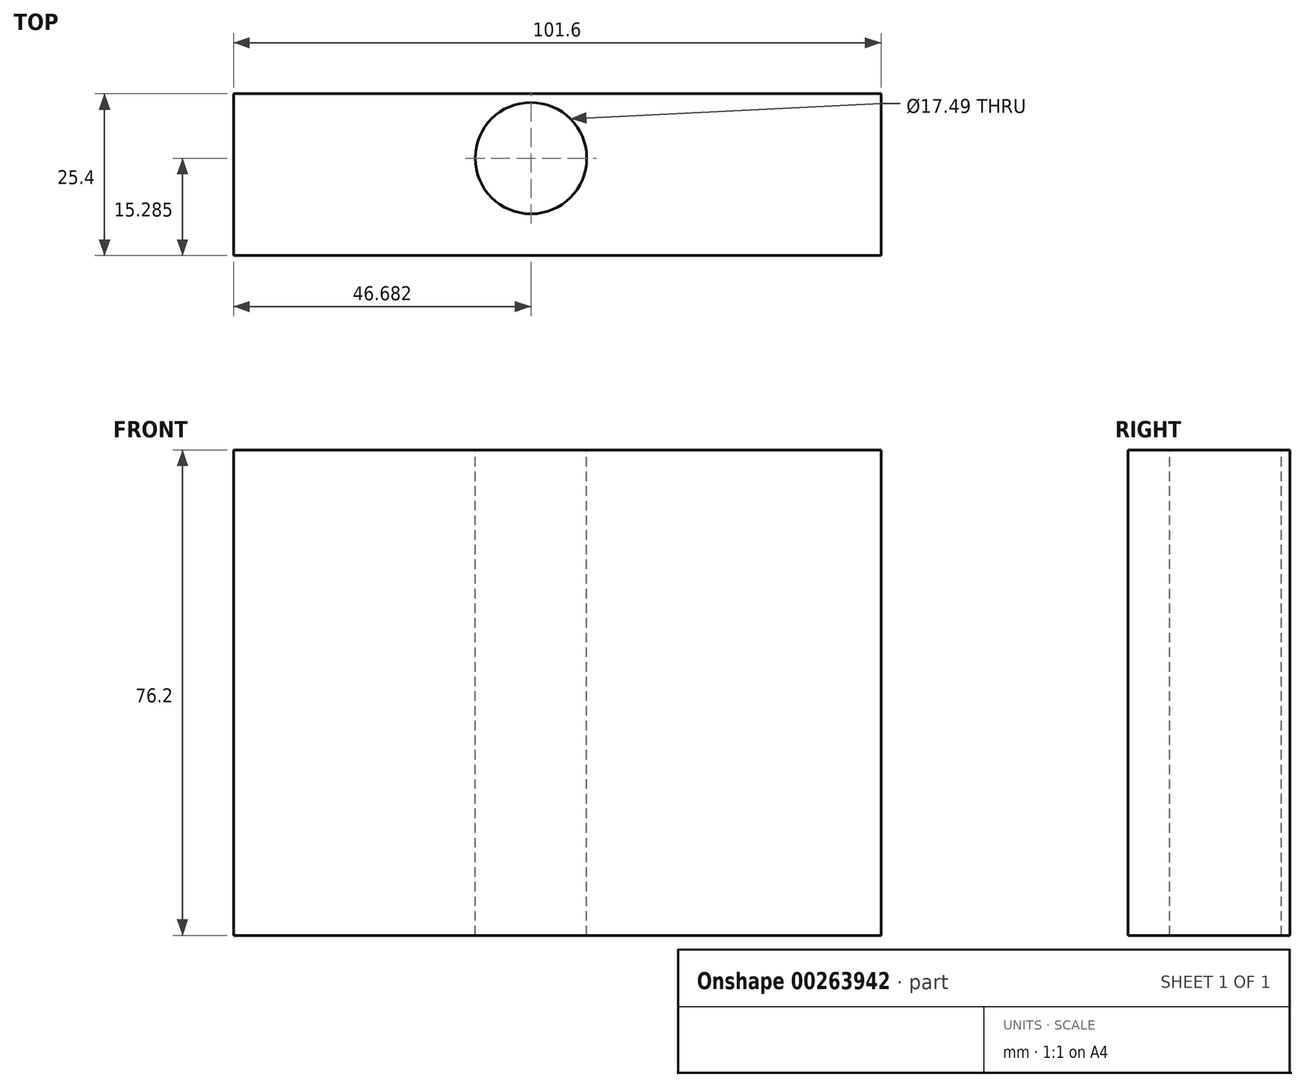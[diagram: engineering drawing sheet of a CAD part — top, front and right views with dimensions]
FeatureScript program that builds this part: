
annotation { "Feature Type Name" : "Feature", "Feature Type Description" : "" }
export const myFeature = defineFeature(function(context is Context, id is Id, definition is map)
    precondition{}
    {
        {
            var Q0;
            Q0=qCreatedBy(makeId("Front.planeOp"),FACE);
            var sketch = newSketch(context, id + "F0", { "sketchPlane" : qUnion([Q0])});
            skLineSegment(sketch, "E0.bottom", {"start": v(0, 0) * mm, "end": v(101.6, 0) * mm});
            skLineSegment(sketch, "E0.top", {"start": v(0, 76.2) * mm, "end": v(101.6, 76.2) * mm});
            skLineSegment(sketch, "E0.left", {"start": v(0, 0) * mm, "end": v(0, 76.2) * mm});
            skLineSegment(sketch, "E0.right", {"start": v(101.6, 0) * mm, "end": v(101.6, 76.2) * mm});
            skSolve(sketch);
        }
        {
            var Q0;
            Q0=makeQuery(id+"F0.imprint","IMPRINT",FACE,{"disambiguationData":[TD([[makeQuery(id+"F0.imprint","IMPRINT",EDGE,{"derivedFrom":sQuery(id+"F0.wireOp",EDGE,"E0.bottom")}),1.0]])]});
            extrude(context, id + "F1", {"entities" : qUnion([Q0]), "depth" : 25.4 * mm});
        }
        {
            var Q0;
            Q0=makeQuery(id+"F1.opExtrude","SWEPT_FACE",FACE,{"disambiguationData":[OSD([sQuery(id+"F0.wireOp",EDGE,"E0.top")])]});
            var sketch = newSketch(context, id + "F2", { "sketchPlane" : qUnion([Q0])});
            skCircle(sketch, "E1", {"center": v(46.68, -10.11) * mm, "radius": 8.75 * mm});
            skSolve(sketch);
        }
        {
            var Q0;
            Q0=makeQuery(id+"F2.imprint","IMPRINT",FACE,{"disambiguationData":[TD([[makeQuery(id+"F2.imprint","IMPRINT",EDGE,{"derivedFrom":sQuery(id+"F2.wireOp",EDGE,"E1")}),1.0]])]});
            extrude(context, id + "F3", {"entities" : qUnion([Q0]), "operationType" : NewBodyOperationType.REMOVE, "endBound" : BoundingType.UP_TO_NEXT, "oppositeDirection" : true, "depth" : 25.4 * mm});
        }
    });
